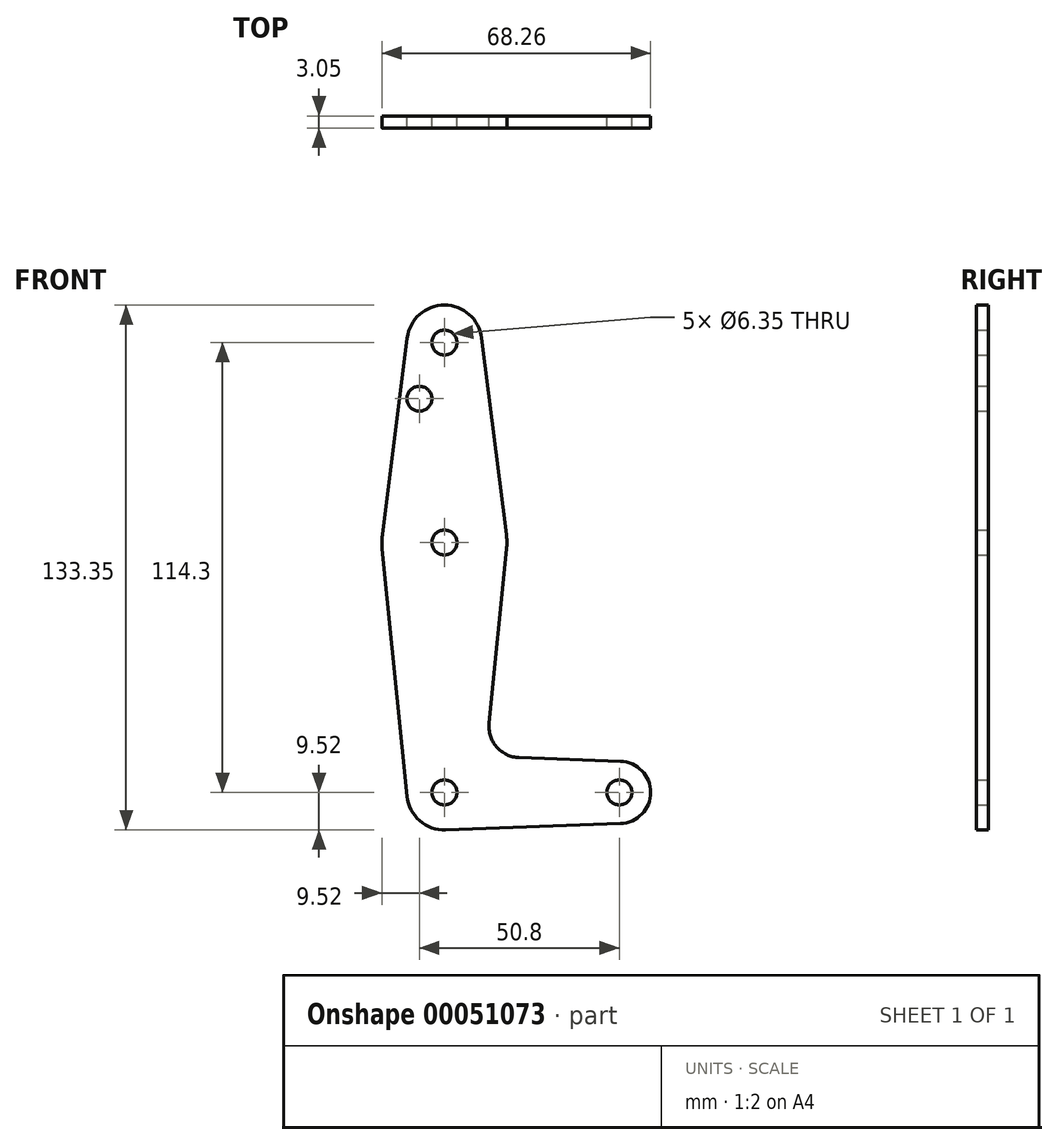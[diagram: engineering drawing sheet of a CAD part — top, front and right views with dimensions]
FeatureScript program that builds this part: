
annotation { "Feature Type Name" : "Feature", "Feature Type Description" : "" }
export const myFeature = defineFeature(function(context is Context, id is Id, definition is map)
    precondition{}
    {
        {
            var Q0;
            Q0=qCreatedBy(makeId("Front.planeOp"),FACE);
            var sketch = newSketch(context, id + "F0", { "sketchPlane" : qUnion([Q0])});
            skCircle(sketch, "E0", {"center": v(0, 114.3) * mm, "radius": 9.53 * mm});
            skCircle(sketch, "E1", {"center": v(0, 63.5) * mm, "radius": 15.88 * mm});
            skCircle(sketch, "E2", {"center": v(0, 0) * mm, "radius": 9.53 * mm});
            skCircle(sketch, "E3", {"center": v(44.45, 0) * mm, "radius": 7.94 * mm});
            skLineSegment(sketch, "E4", {"start": v(0, 114.3) * mm, "end": v(0, 63.5) * mm, "construction": true});
            skLineSegment(sketch, "E5", {"start": v(0, 0) * mm, "end": v(0, 63.5) * mm, "construction": true});
            skLineSegment(sketch, "E6", {"start": v(0, 0) * mm, "end": v(44.45, 0) * mm, "construction": true});
            skLineSegment(sketch, "E7", {"start": v(-9.45, 115.5) * mm, "end": v(-15.75, 65.48) * mm});
            skLineSegment(sketch, "E8", {"start": v(9.45, 115.5) * mm, "end": v(15.75, 65.48) * mm});
            skCircle(sketch, "E9", {"center": v(0, 114.3) * mm, "radius": 3.18 * mm});
            skCircle(sketch, "E10", {"center": v(0, 63.5) * mm, "radius": 3.18 * mm});
            skCircle(sketch, "E11", {"center": v(0, 0) * mm, "radius": 3.18 * mm});
            skCircle(sketch, "E12", {"center": v(44.45, 0) * mm, "radius": 3.18 * mm});
            skCircle(sketch, "E13", {"center": v(-6.35, 100.03) * mm, "radius": 3.18 * mm});
            skLineSegment(sketch, "E14", {"start": v(0.34, -9.52) * mm, "end": v(44.73, -7.93) * mm});
            skLineSegment(sketch, "E15", {"start": v(18.97, 8.85) * mm, "end": v(44.73, 7.93) * mm});
            skLineSegment(sketch, "E16", {"start": v(-15.8, 61.91) * mm, "end": v(-9.48, -0.95) * mm});
            skLineSegment(sketch, "E17", {"start": v(15.8, 61.91) * mm, "end": v(11.34, 17.6) * mm});
            skPoint(sketch, "E18.newPointA", {"position": v(9.57, 0) * mm});
            skArc(sketch, "E18.filletArc", {"start": v(11.34, 17.6) * mm, "mid": v(13.26, 11.57) * mm, "end": v(18.97, 8.85) * mm});
            skSolve(sketch);
        }
        {
            var Q0;
            Q0 = qSketchRegion(id + "F0", true);
            extrude(context, id + "F1", {"entities" : qUnion([Q0]), "depth" : 3.05 * mm});
        }
    });
